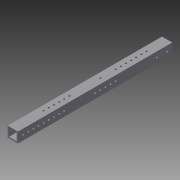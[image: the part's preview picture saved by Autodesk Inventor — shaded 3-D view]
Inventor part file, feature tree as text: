
AUTODESK INVENTOR PART (.ipt)
format: ipt  version: 2014 (Build 180170000, 170)  size: 169,984 bytes
history: native  units: in
note: dims shown in document units (in); Inventor stores cm internally (conversion verified against a paired STEP export)
features: extrude x3, sketch x3
ambient origin geometry x8: Origin, YZ Plane, XZ Plane, XY Plane, X Axis, Y Axis, Z Axis, Center Point
bodies: Solid1 (feature_tree)
feature tree (6):
  extrude  "Extrusion1"  Depth=1.0in
  extrude  "Extrusion2"  Depth=15.0in TaperAngle=0.0deg
  extrude  "Extrusion3"  Depth=15.0in
  sketch  "Sketch1"  dims[d0=1.0in d1=1.0in]
  sketch  "Sketch2"  dims[d2=0.125in d3=15.0in d4=0.0in]
  sketch  "Sketch3"  dims[d5=0.163in d6=0.5in d7=0.5in d8=3.5433in d10=0.5in d11=0.3937in d13=1.0in d15=3.0in d16=0.5in d17=1.9685in d19=0.5in d20=0.3937in d22=1.0in d24=0.5in d25=0.5in d26=0.7874in d28=1.0in d29=0.3937in d31=1.0in d33=15.0in d34=0.0in d35=0.163in d36=3.0in d37=0.5in d38=2.3622in d40=0.5in d41=0.3937in d43=1.0in d45=2.0in d46=0.5in d47=2.7559in d49=0.5in d50=0.3937in d52=1.0in d54=1.5in d55=0.5in d56=15.0in d57=0.0in]
